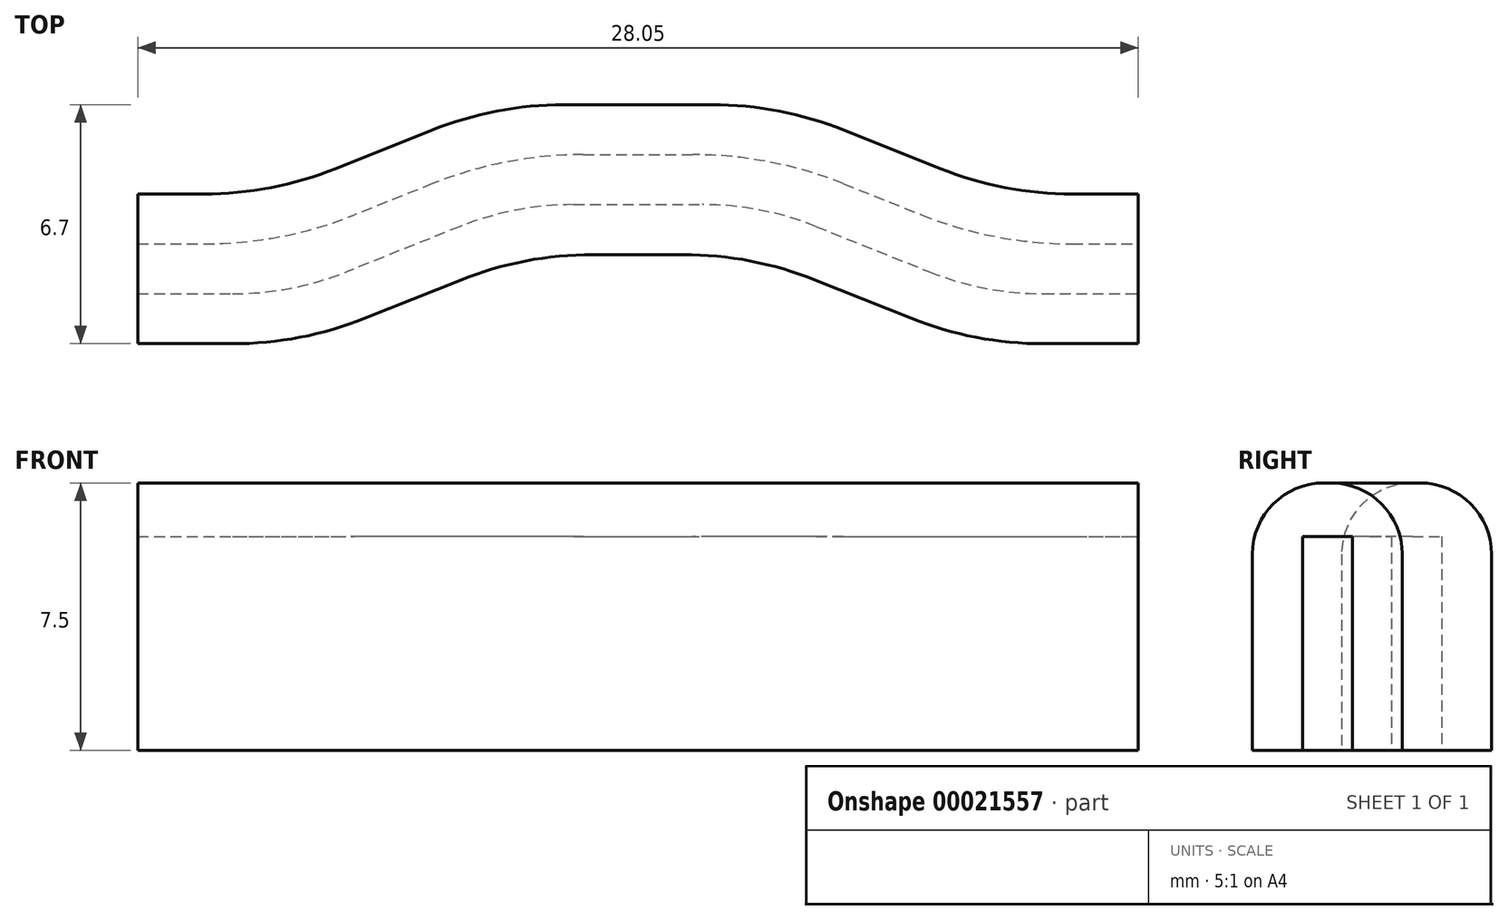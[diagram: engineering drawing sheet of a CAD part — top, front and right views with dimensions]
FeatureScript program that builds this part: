
annotation { "Feature Type Name" : "Feature", "Feature Type Description" : "" }
export const myFeature = defineFeature(function(context is Context, id is Id, definition is map)
    precondition{}
    {
        {
            var Q0;
            Q0=qCreatedBy(makeId("Top.planeOp"),FACE);
            var sketch = newSketch(context, id + "F0", { "sketchPlane" : qUnion([Q0])});
            skLineSegment(sketch, "E0.bottom", {"start": v(0, 0) * mm, "end": v(4.3, 0) * mm});
            skLineSegment(sketch, "E0.top", {"start": v(0, 1.4) * mm, "end": v(4.04, 1.4) * mm});
            skLineSegment(sketch, "E1", {"start": v(10.3, 3.9) * mm, "end": v(17.75, 3.9) * mm});
            skLineSegment(sketch, "E2", {"start": v(10.3, 3.9) * mm, "end": v(4.04, 1.4) * mm});
            skLineSegment(sketch, "E3", {"start": v(17.75, 3.9) * mm, "end": v(24, 1.4) * mm});
            skLineSegment(sketch, "E4.0", {"start": v(10.57, 2.5) * mm, "end": v(4.3, 0) * mm});
            skLineSegment(sketch, "E4.1", {"start": v(10.57, 2.5) * mm, "end": v(17.48, 2.5) * mm});
            skLineSegment(sketch, "E4.2", {"start": v(17.48, 2.5) * mm, "end": v(23.74, 0) * mm});
            skLineSegment(sketch, "E5.trimOffspring", {"start": v(24, 1.4) * mm, "end": v(28.05, 1.4) * mm});
            skLineSegment(sketch, "E6.trimOffspring", {"start": v(23.74, 0) * mm, "end": v(28.05, 0) * mm});
            skPoint(sketch, "E7.orphan", {"position": v(14.02, 0) * mm});
            skPoint(sketch, "E8.start.orphan", {"position": v(14.02, 3.9) * mm});
            skLineSegment(sketch, "E9.0", {"start": v(24.28, 2.8) * mm, "end": v(28.05, 2.8) * mm});
            skLineSegment(sketch, "E9.1", {"start": v(18.02, 5.3) * mm, "end": v(24.28, 2.8) * mm});
            skLineSegment(sketch, "E9.2", {"start": v(10.03, 5.3) * mm, "end": v(18.02, 5.3) * mm});
            skLineSegment(sketch, "E9.3", {"start": v(10.03, 5.3) * mm, "end": v(3.77, 2.8) * mm});
            skLineSegment(sketch, "E9.4", {"start": v(0, 2.8) * mm, "end": v(3.77, 2.8) * mm});
            skLineSegment(sketch, "E10.0", {"start": v(23.47, -1.4) * mm, "end": v(28.05, -1.4) * mm});
            skLineSegment(sketch, "E10.1", {"start": v(17.2, 1.1) * mm, "end": v(23.47, -1.4) * mm});
            skLineSegment(sketch, "E10.2", {"start": v(10.84, 1.1) * mm, "end": v(17.2, 1.1) * mm});
            skLineSegment(sketch, "E10.3", {"start": v(10.84, 1.1) * mm, "end": v(4.58, -1.4) * mm});
            skLineSegment(sketch, "E10.4", {"start": v(0, -1.4) * mm, "end": v(4.58, -1.4) * mm});
            skLineSegment(sketch, "E11", {"start": v(0, 2.8) * mm, "end": v(0, 1.4) * mm});
            skLineSegment(sketch, "E12", {"start": v(0, 0) * mm, "end": v(0, -1.4) * mm});
            skLineSegment(sketch, "E13", {"start": v(28.05, 0) * mm, "end": v(28.05, -1.4) * mm});
            skLineSegment(sketch, "E14", {"start": v(28.05, 2.8) * mm, "end": v(28.05, 1.4) * mm});
            skSolve(sketch);
        }
        {
            var Q0;
            Q0 = qSketchRegion(id + "F0", true);
            extrude(context, id + "F1", {"entities" : qUnion([Q0]), "depth" : 6 * mm});
        }
        {
            var Q0;
            Q0=makeQuery(id+"F1.opExtrude","CAP_FACE",FACE,{"disambiguationData":[OSD([sQuery(id+"F0.wireOp",EDGE,"E0.top"),sQuery(id+"F0.wireOp",EDGE,"E1"),sQuery(id+"F0.wireOp",EDGE,"E2"),sQuery(id+"F0.wireOp",EDGE,"E3"),sQuery(id+"F0.wireOp",EDGE,"E5.trimOffspring"),sQuery(id+"F0.wireOp",EDGE,"E9.0"),sQuery(id+"F0.wireOp",EDGE,"E9.1"),sQuery(id+"F0.wireOp",EDGE,"E9.2"),sQuery(id+"F0.wireOp",EDGE,"E9.3"),sQuery(id+"F0.wireOp",EDGE,"E9.4"),sQuery(id+"F0.wireOp",EDGE,"E11"),sQuery(id+"F0.wireOp",EDGE,"E14")])],"isStart":false});
            var sketch = newSketch(context, id + "F2", { "sketchPlane" : qUnion([Q0])});
            skLineSegment(sketch, "E15.0", {"start": v(24.28, 2.8) * mm, "end": v(28.05, 2.8) * mm});
            skLineSegment(sketch, "E15.1", {"start": v(18.02, 5.3) * mm, "end": v(24.28, 2.8) * mm});
            skLineSegment(sketch, "E15.2", {"start": v(10.03, 5.3) * mm, "end": v(18.02, 5.3) * mm});
            skLineSegment(sketch, "E15.3", {"start": v(10.03, 5.3) * mm, "end": v(3.77, 2.8) * mm});
            skLineSegment(sketch, "E15.4", {"start": v(0, 2.8) * mm, "end": v(3.77, 2.8) * mm});
            skLineSegment(sketch, "E16.0", {"start": v(23.47, -1.4) * mm, "end": v(28.05, -1.4) * mm});
            skLineSegment(sketch, "E16.1", {"start": v(17.2, 1.1) * mm, "end": v(23.47, -1.4) * mm});
            skLineSegment(sketch, "E16.2", {"start": v(10.84, 1.1) * mm, "end": v(17.2, 1.1) * mm});
            skLineSegment(sketch, "E16.3", {"start": v(10.84, 1.1) * mm, "end": v(4.58, -1.4) * mm});
            skLineSegment(sketch, "E16.4", {"start": v(0, -1.4) * mm, "end": v(4.58, -1.4) * mm});
            skLineSegment(sketch, "E17", {"start": v(0, 2.8) * mm, "end": v(0, -1.4) * mm});
            skLineSegment(sketch, "E18", {"start": v(28.05, 2.8) * mm, "end": v(28.05, -1.4) * mm});
            skSolve(sketch);
        }
        {
            var Q0;
            Q0 = qSketchRegion(id + "F2", true);
            extrude(context, id + "F3", {"entities" : qUnion([Q0]), "operationType" : NewBodyOperationType.ADD, "depth" : 1.5 * mm});
        }
        {
            var Q0;
            Q0=makeQuery(id+"F3.boolean.opBoolean","MERGE",EDGE,{"derivedFrom":[makeQuery(id+"F1.opExtrude","SWEPT_EDGE",EDGE,{"disambiguationData":[OSD([sQuery(id+"F0.wireOp",EDGE,"E10.3"),sQuery(id+"F0.wireOp",EDGE,"E10.4")])]}),makeQuery(id+"F3.opExtrude","SWEPT_EDGE",EDGE,{"disambiguationData":[OSD([sQuery(id+"F2.wireOp",EDGE,"E16.3"),sQuery(id+"F2.wireOp",EDGE,"E16.4")])]})]});
            var Q1;
            Q1=makeQuery(id+"F3.boolean.opBoolean","MERGE",EDGE,{"derivedFrom":[makeQuery(id+"F1.opExtrude","SWEPT_EDGE",EDGE,{"disambiguationData":[OSD([sQuery(id+"F0.wireOp",EDGE,"E10.2"),sQuery(id+"F0.wireOp",EDGE,"E10.3")])]}),makeQuery(id+"F3.opExtrude","SWEPT_EDGE",EDGE,{"disambiguationData":[OSD([sQuery(id+"F2.wireOp",EDGE,"E16.2"),sQuery(id+"F2.wireOp",EDGE,"E16.3")])]})]});
            var Q2;
            Q2=makeQuery(id+"F3.boolean.opBoolean","MERGE",EDGE,{"derivedFrom":[makeQuery(id+"F1.opExtrude","SWEPT_EDGE",EDGE,{"disambiguationData":[OSD([sQuery(id+"F0.wireOp",EDGE,"E10.1"),sQuery(id+"F0.wireOp",EDGE,"E10.2")])]}),makeQuery(id+"F3.opExtrude","SWEPT_EDGE",EDGE,{"disambiguationData":[OSD([sQuery(id+"F2.wireOp",EDGE,"E16.1"),sQuery(id+"F2.wireOp",EDGE,"E16.2")])]})]});
            var Q3;
            Q3=makeQuery(id+"F3.boolean.opBoolean","MERGE",EDGE,{"derivedFrom":[makeQuery(id+"F1.opExtrude","SWEPT_EDGE",EDGE,{"disambiguationData":[OSD([sQuery(id+"F0.wireOp",EDGE,"E10.0"),sQuery(id+"F0.wireOp",EDGE,"E10.1")])]}),makeQuery(id+"F3.opExtrude","SWEPT_EDGE",EDGE,{"disambiguationData":[OSD([sQuery(id+"F2.wireOp",EDGE,"E16.0"),sQuery(id+"F2.wireOp",EDGE,"E16.1")])]})]});
            var Q4;
            Q4=makeQuery(id+"F3.boolean.opBoolean","MERGE",EDGE,{"derivedFrom":[makeQuery(id+"F1.opExtrude","SWEPT_EDGE",EDGE,{"disambiguationData":[OSD([sQuery(id+"F0.wireOp",EDGE,"E9.3"),sQuery(id+"F0.wireOp",EDGE,"E9.4")])]}),makeQuery(id+"F3.opExtrude","SWEPT_EDGE",EDGE,{"disambiguationData":[OSD([sQuery(id+"F2.wireOp",EDGE,"E15.3"),sQuery(id+"F2.wireOp",EDGE,"E15.4")])]})]});
            var Q5;
            Q5=makeQuery(id+"F3.boolean.opBoolean","MERGE",EDGE,{"derivedFrom":[makeQuery(id+"F1.opExtrude","SWEPT_EDGE",EDGE,{"disambiguationData":[OSD([sQuery(id+"F0.wireOp",EDGE,"E9.2"),sQuery(id+"F0.wireOp",EDGE,"E9.3")])]}),makeQuery(id+"F3.opExtrude","SWEPT_EDGE",EDGE,{"disambiguationData":[OSD([sQuery(id+"F2.wireOp",EDGE,"E15.2"),sQuery(id+"F2.wireOp",EDGE,"E15.3")])]})]});
            var Q6;
            Q6=makeQuery(id+"F3.boolean.opBoolean","MERGE",EDGE,{"derivedFrom":[makeQuery(id+"F1.opExtrude","SWEPT_EDGE",EDGE,{"disambiguationData":[OSD([sQuery(id+"F0.wireOp",EDGE,"E9.1"),sQuery(id+"F0.wireOp",EDGE,"E9.2")])]}),makeQuery(id+"F3.opExtrude","SWEPT_EDGE",EDGE,{"disambiguationData":[OSD([sQuery(id+"F2.wireOp",EDGE,"E15.1"),sQuery(id+"F2.wireOp",EDGE,"E15.2")])]})]});
            var Q7;
            Q7=makeQuery(id+"F3.boolean.opBoolean","MERGE",EDGE,{"derivedFrom":[makeQuery(id+"F1.opExtrude","SWEPT_EDGE",EDGE,{"disambiguationData":[OSD([sQuery(id+"F0.wireOp",EDGE,"E9.0"),sQuery(id+"F0.wireOp",EDGE,"E9.1")])]}),makeQuery(id+"F3.opExtrude","SWEPT_EDGE",EDGE,{"disambiguationData":[OSD([sQuery(id+"F2.wireOp",EDGE,"E15.0"),sQuery(id+"F2.wireOp",EDGE,"E15.1")])]})]});
            fillet(context, id + "F4", {"entities" : qUnion([Q0, Q1, Q2, Q3, Q4, Q5, Q6, Q7]), "radius" : 10 * mm, "tangentPropagation" : true, "allowEdgeOverflow" : false});
        }
        {
            var Q0;
            Q0=makeQuery(id+"F1.opExtrude","SWEPT_EDGE",EDGE,{"disambiguationData":[OSD([sQuery(id+"F0.wireOp",EDGE,"E0.bottom"),sQuery(id+"F0.wireOp",EDGE,"E4.0")])]});
            var Q1;
            Q1=makeQuery(id+"F1.opExtrude","SWEPT_EDGE",EDGE,{"disambiguationData":[OSD([sQuery(id+"F0.wireOp",EDGE,"E4.0"),sQuery(id+"F0.wireOp",EDGE,"E4.1")])]});
            var Q2;
            Q2=makeQuery(id+"F1.opExtrude","SWEPT_EDGE",EDGE,{"disambiguationData":[OSD([sQuery(id+"F0.wireOp",EDGE,"E4.1"),sQuery(id+"F0.wireOp",EDGE,"E4.2")])]});
            var Q3;
            Q3=makeQuery(id+"F1.opExtrude","SWEPT_EDGE",EDGE,{"disambiguationData":[OSD([sQuery(id+"F0.wireOp",EDGE,"E4.2"),sQuery(id+"F0.wireOp",EDGE,"E6.trimOffspring")])]});
            fillet(context, id + "F5", {"entities" : qUnion([Q0, Q1, Q2, Q3]), "radius" : (10 - 1.4) * mm, "tangentPropagation" : true, "allowEdgeOverflow" : false});
        }
        {
            var Q0;
            Q0=makeQuery(id+"F1.opExtrude","SWEPT_EDGE",EDGE,{"disambiguationData":[OSD([sQuery(id+"F0.wireOp",EDGE,"E0.top"),sQuery(id+"F0.wireOp",EDGE,"E2")])]});
            var Q1;
            Q1=makeQuery(id+"F1.opExtrude","SWEPT_EDGE",EDGE,{"disambiguationData":[OSD([sQuery(id+"F0.wireOp",EDGE,"E1"),sQuery(id+"F0.wireOp",EDGE,"E2")])]});
            var Q2;
            Q2=makeQuery(id+"F1.opExtrude","SWEPT_EDGE",EDGE,{"disambiguationData":[OSD([sQuery(id+"F0.wireOp",EDGE,"E1"),sQuery(id+"F0.wireOp",EDGE,"E3")])]});
            var Q3;
            Q3=makeQuery(id+"F1.opExtrude","SWEPT_EDGE",EDGE,{"disambiguationData":[OSD([sQuery(id+"F0.wireOp",EDGE,"E3"),sQuery(id+"F0.wireOp",EDGE,"E5.trimOffspring")])]});
            fillet(context, id + "F6", {"entities" : qUnion([Q0, Q1, Q2, Q3]), "radius" : 11.4 * mm, "tangentPropagation" : true, "allowEdgeOverflow" : false});
        }
        {
            var Q0;
            Q0=makeQuery(id+"F3.opExtrude","CAP_EDGE",EDGE,{"disambiguationData":[OSD([sQuery(id+"F2.wireOp",EDGE,"E16.4")])],"isStart":false});
            var Q1;
            Q1=makeQuery(id+"F3.opExtrude","CAP_EDGE",EDGE,{"disambiguationData":[OSD([sQuery(id+"F2.wireOp",EDGE,"E15.4")])],"isStart":false});
            fillet(context, id + "F7", {"entities" : qUnion([Q0, Q1]), "radius" : 2 * mm, "tangentPropagation" : true, "allowEdgeOverflow" : false});
        }
    });
